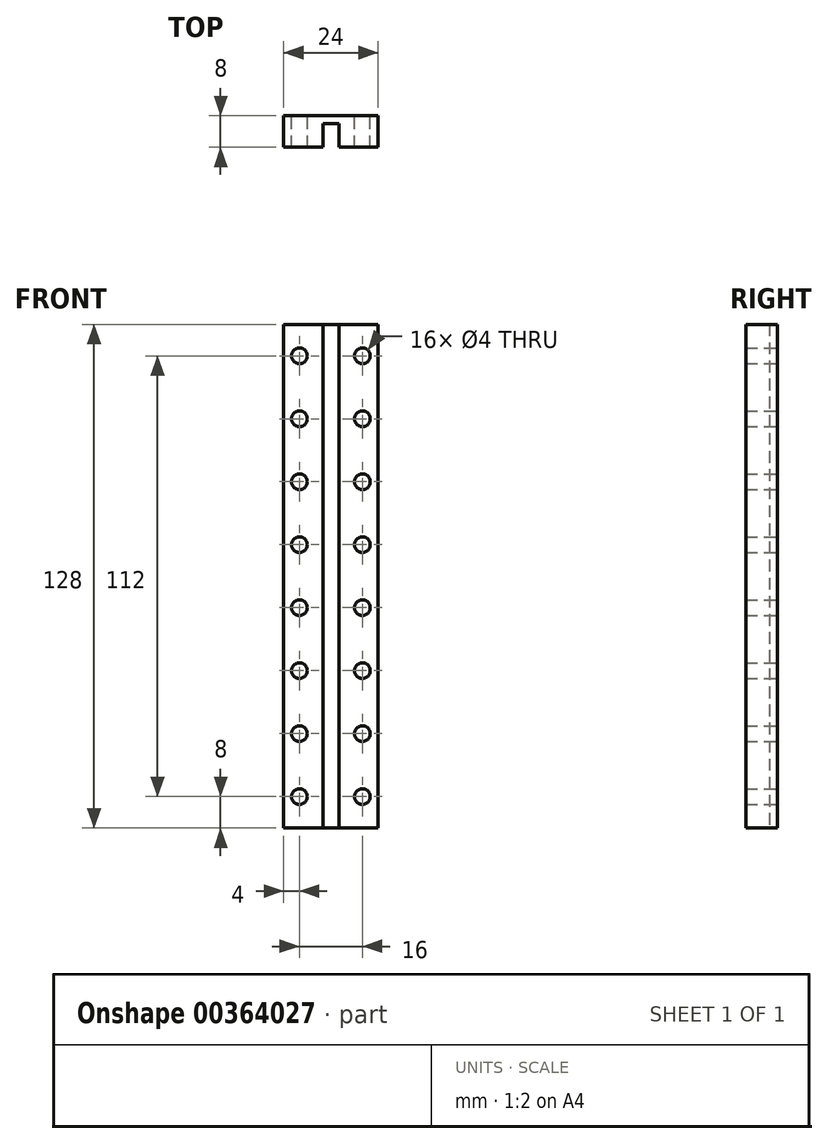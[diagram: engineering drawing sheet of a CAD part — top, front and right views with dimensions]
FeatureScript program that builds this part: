
annotation { "Feature Type Name" : "Feature", "Feature Type Description" : "" }
export const myFeature = defineFeature(function(context is Context, id is Id, definition is map)
    precondition{}
    {
        {
            var Q0;
            Q0=qCreatedBy(makeId("Top.planeOp"),FACE);
            var sketch = newSketch(context, id + "F0", { "sketchPlane" : qUnion([Q0])});
            skLineSegment(sketch, "E0.top", {"start": v(12, 4) * mm, "end": v(-12, 4) * mm});
            skLineSegment(sketch, "E0.left", {"start": v(12, -4) * mm, "end": v(12, 4) * mm});
            skLineSegment(sketch, "E0.right", {"start": v(-12, -4) * mm, "end": v(-12, 4) * mm});
            skPoint(sketch, "E0.middle", {"position": v(0, 0) * mm});
            skLineSegment(sketch, "E1", {"start": v(-12, -4) * mm, "end": v(-2, -4) * mm});
            skLineSegment(sketch, "E2", {"start": v(-2, -4) * mm, "end": v(-2, 2) * mm});
            skLineSegment(sketch, "E3", {"start": v(-2, 2) * mm, "end": v(2, 2) * mm});
            skLineSegment(sketch, "E4", {"start": v(2, 2) * mm, "end": v(2, -4) * mm});
            skLineSegment(sketch, "E5", {"start": v(2, -4) * mm, "end": v(12, -4) * mm});
            skSolve(sketch);
        }
        {
            var Q0;
            Q0=qSketchRegion(id+"F0",true);
            extrude(context, id + "F1", {"entities" : qUnion([Q0]), "depth" : 128 * mm, "offsetDistance" : 25 * mm});
        }
        {
            var Q0;
            Q0=makeQuery(id+"F1.opExtrude","SWEPT_FACE",FACE,{"disambiguationData":[OSD([sQuery(id+"F0.wireOp",EDGE,"E0.top")])]});
            var sketch = newSketch(context, id + "F2", { "sketchPlane" : qUnion([Q0])});
            skLineSegment(sketch, "E6", {"start": v(-8, 0) * mm, "end": v(-8, 8) * mm, "construction": true});
            skCircle(sketch, "E7", {"center": v(-8, 8) * mm, "radius": 2 * mm});
            skCircle(sketch, "E8.0.1.0", {"center": v(-8, 24) * mm, "radius": 2 * mm});
            skCircle(sketch, "E8.0.2.0", {"center": v(-8, 40) * mm, "radius": 2 * mm});
            skCircle(sketch, "E8.0.3.0", {"center": v(-8, 56) * mm, "radius": 2 * mm});
            skCircle(sketch, "E8.0.4.0", {"center": v(-8, 72) * mm, "radius": 2 * mm});
            skCircle(sketch, "E8.1.0.0", {"center": v(8, 8) * mm, "radius": 2 * mm});
            skCircle(sketch, "E8.1.1.0", {"center": v(8, 24) * mm, "radius": 2 * mm});
            skCircle(sketch, "E8.1.2.0", {"center": v(8, 40) * mm, "radius": 2 * mm});
            skCircle(sketch, "E8.1.3.0", {"center": v(8, 56) * mm, "radius": 2 * mm});
            skCircle(sketch, "E8.1.4.0", {"center": v(8, 72) * mm, "radius": 2 * mm});
            skLineSegment(sketch, "E8.direction1", {"start": v(-8, 8) * mm, "end": v(8, 8) * mm, "construction": true});
            skLineSegment(sketch, "E8.direction2", {"start": v(-8, 8) * mm, "end": v(-8, 24) * mm, "construction": true});
            skCircle(sketch, "E9.0.0.5", {"center": v(-8, 88) * mm, "radius": 2 * mm});
            skCircle(sketch, "E9.0.0.6", {"center": v(-8, 104) * mm, "radius": 2 * mm});
            skCircle(sketch, "E9.0.0.7", {"center": v(-8, 120) * mm, "radius": 2 * mm});
            skCircle(sketch, "E9.0.1.5", {"center": v(8, 88) * mm, "radius": 2 * mm});
            skCircle(sketch, "E9.0.1.6", {"center": v(8, 104) * mm, "radius": 2 * mm});
            skCircle(sketch, "E9.0.1.7", {"center": v(8, 120) * mm, "radius": 2 * mm});
            skSolve(sketch);
        }
        {
            var Q0;
            Q0=qSketchRegion(id+"F2",true);
            extrude(context, id + "F3", {"entities" : qUnion([Q0]), "operationType" : NewBodyOperationType.REMOVE, "oppositeDirection" : true, "depth" : 25 * mm});
        }
    });
